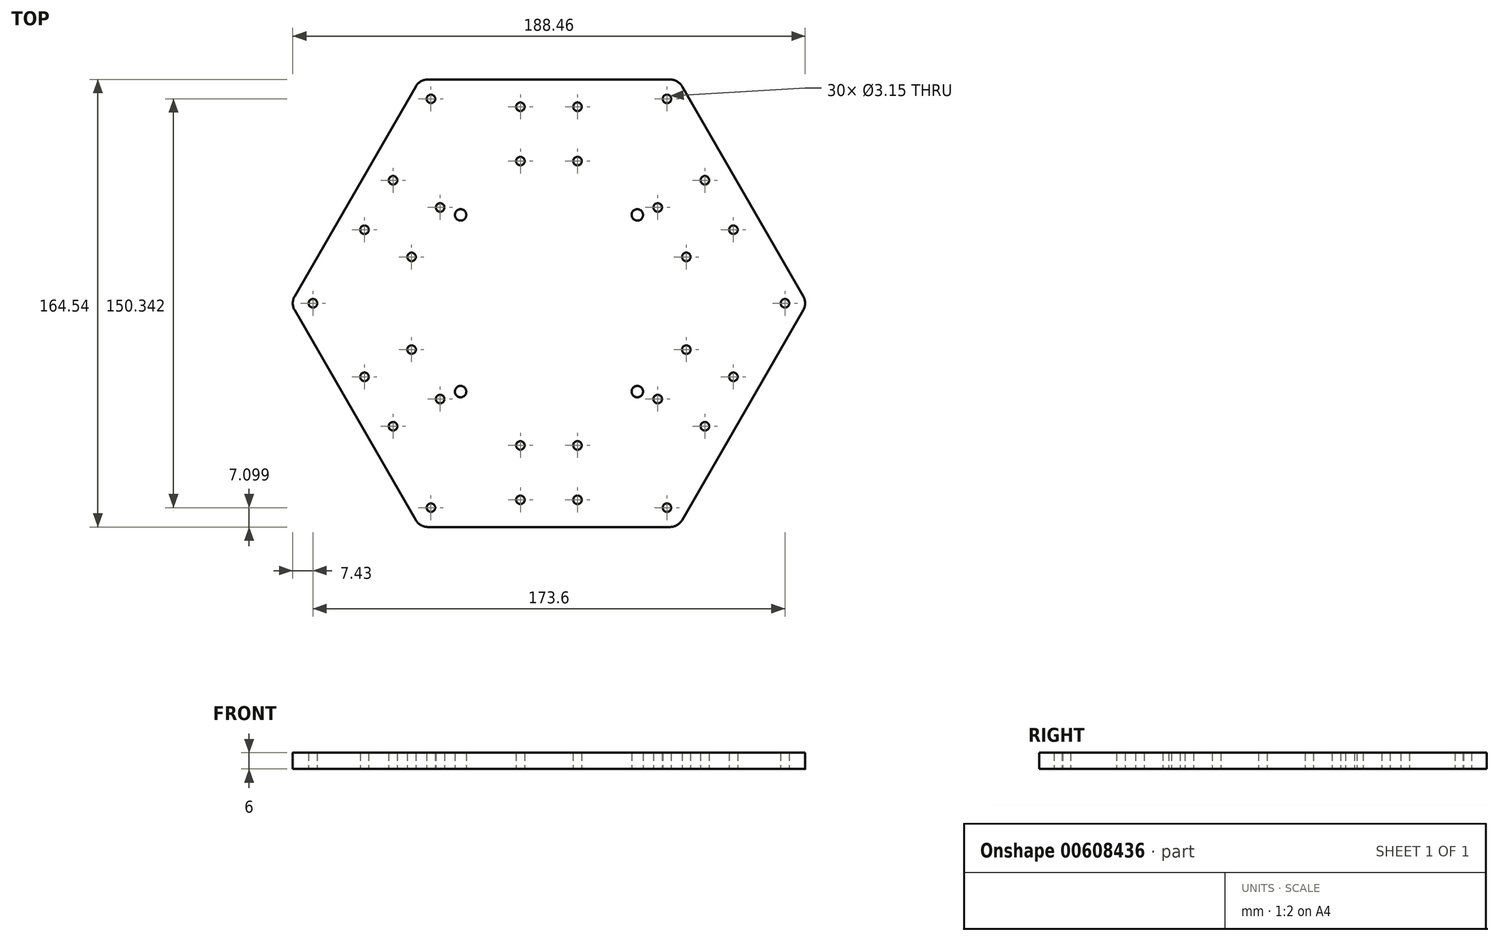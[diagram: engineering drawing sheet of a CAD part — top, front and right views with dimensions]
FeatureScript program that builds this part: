
annotation { "Feature Type Name" : "Feature", "Feature Type Description" : "" }
export const myFeature = defineFeature(function(context is Context, id is Id, definition is map)
    precondition{}
    {
        {
            var Q0;
            Q0=qCreatedBy(makeId("Top.planeOp"),FACE);
            var sketch = newSketch(context, id + "F0", { "sketchPlane" : qUnion([Q0])});
            skLineSegment(sketch, "E0.1", {"start": v(-48.94, -79.77) * mm, "end": v(-93.56, -2.5) * mm});
            skLineSegment(sketch, "E0.2", {"start": v(-93.56, 2.5) * mm, "end": v(-48.94, 79.77) * mm});
            skLineSegment(sketch, "E0.3", {"start": v(-44.61, 82.27) * mm, "end": v(44.61, 82.27) * mm});
            skLineSegment(sketch, "E0.4", {"start": v(48.94, 79.77) * mm, "end": v(93.56, 2.5) * mm});
            skLineSegment(sketch, "E0.5", {"start": v(93.56, -2.5) * mm, "end": v(48.94, -79.77) * mm});
            skPoint(sketch, "E0.cCircle.center.orphan", {"position": v(0, 0) * mm});
            skLineSegment(sketch, "E1", {"start": v(-44.61, -82.27) * mm, "end": v(44.61, -82.27) * mm});
            skPoint(sketch, "E2", {"position": v(-47.5, 82.27) * mm});
            skPoint(sketch, "E3", {"position": v(-43.4, 75.17) * mm});
            skCircle(sketch, "E4", {"center": v(-43.4, 75.17) * mm, "radius": 1.57 * mm});
            skCircle(sketch, "E5.1.0", {"center": v(-86.8, 0) * mm, "radius": 1.57 * mm});
            skCircle(sketch, "E5.2.0", {"center": v(-43.4, -75.17) * mm, "radius": 1.57 * mm});
            skCircle(sketch, "E5.3.0", {"center": v(43.4, -75.17) * mm, "radius": 1.57 * mm});
            skCircle(sketch, "E5.4.0", {"center": v(86.8, 0) * mm, "radius": 1.57 * mm});
            skCircle(sketch, "E5.5.0", {"center": v(43.4, 75.17) * mm, "radius": 1.57 * mm});
            skPoint(sketch, "E6", {"position": v(47.5, 82.27) * mm});
            skPoint(sketch, "E7", {"position": v(0, 82.27) * mm});
            skPoint(sketch, "E8", {"position": v(10.5, 82.27) * mm});
            skPoint(sketch, "E9", {"position": v(-10.5, 82.27) * mm});
            skPoint(sketch, "E10", {"position": v(-10.5, 72.27) * mm});
            skPoint(sketch, "E11", {"position": v(10.5, 72.27) * mm});
            skPoint(sketch, "E12", {"position": v(-10.5, 52.27) * mm});
            skPoint(sketch, "E13", {"position": v(10.5, 52.27) * mm});
            skCircle(sketch, "E14", {"center": v(-10.5, 72.27) * mm, "radius": 1.57 * mm});
            skCircle(sketch, "E15", {"center": v(10.5, 72.27) * mm, "radius": 1.57 * mm});
            skCircle(sketch, "E16", {"center": v(10.5, 52.27) * mm, "radius": 1.57 * mm});
            skCircle(sketch, "E17", {"center": v(-10.5, 52.27) * mm, "radius": 1.57 * mm});
            skPoint(sketch, "E18.1.0", {"position": v(-57.34, 45.23) * mm});
            skCircle(sketch, "E18.1.1", {"center": v(-57.34, 45.23) * mm, "radius": 1.57 * mm});
            skPoint(sketch, "E18.1.2", {"position": v(-67.84, 27.04) * mm});
            skCircle(sketch, "E18.1.3", {"center": v(-67.84, 27.04) * mm, "radius": 1.57 * mm});
            skPoint(sketch, "E18.1.4", {"position": v(-50.52, 17.04) * mm});
            skCircle(sketch, "E18.1.5", {"center": v(-50.52, 17.04) * mm, "radius": 1.57 * mm});
            skPoint(sketch, "E18.1.6", {"position": v(-40.02, 35.23) * mm});
            skCircle(sketch, "E18.1.7", {"center": v(-40.02, 35.23) * mm, "radius": 1.57 * mm});
            skPoint(sketch, "E18.2.0", {"position": v(-67.84, -27.04) * mm});
            skCircle(sketch, "E18.2.1", {"center": v(-67.84, -27.04) * mm, "radius": 1.57 * mm});
            skPoint(sketch, "E18.2.2", {"position": v(-57.34, -45.23) * mm});
            skCircle(sketch, "E18.2.3", {"center": v(-57.34, -45.23) * mm, "radius": 1.57 * mm});
            skPoint(sketch, "E18.2.4", {"position": v(-40.02, -35.23) * mm});
            skCircle(sketch, "E18.2.5", {"center": v(-40.02, -35.23) * mm, "radius": 1.57 * mm});
            skPoint(sketch, "E18.2.6", {"position": v(-50.52, -17.04) * mm});
            skCircle(sketch, "E18.2.7", {"center": v(-50.52, -17.04) * mm, "radius": 1.57 * mm});
            skPoint(sketch, "E18.3.0", {"position": v(-10.5, -72.27) * mm});
            skCircle(sketch, "E18.3.1", {"center": v(-10.5, -72.27) * mm, "radius": 1.57 * mm});
            skPoint(sketch, "E18.3.2", {"position": v(10.5, -72.27) * mm});
            skCircle(sketch, "E18.3.3", {"center": v(10.5, -72.27) * mm, "radius": 1.57 * mm});
            skPoint(sketch, "E18.3.4", {"position": v(10.5, -52.27) * mm});
            skCircle(sketch, "E18.3.5", {"center": v(10.5, -52.27) * mm, "radius": 1.57 * mm});
            skPoint(sketch, "E18.3.6", {"position": v(-10.5, -52.27) * mm});
            skCircle(sketch, "E18.3.7", {"center": v(-10.5, -52.27) * mm, "radius": 1.57 * mm});
            skPoint(sketch, "E18.4.0", {"position": v(57.34, -45.23) * mm});
            skCircle(sketch, "E18.4.1", {"center": v(57.34, -45.23) * mm, "radius": 1.57 * mm});
            skPoint(sketch, "E18.4.2", {"position": v(67.84, -27.04) * mm});
            skCircle(sketch, "E18.4.3", {"center": v(67.84, -27.04) * mm, "radius": 1.57 * mm});
            skPoint(sketch, "E18.4.4", {"position": v(50.52, -17.04) * mm});
            skCircle(sketch, "E18.4.5", {"center": v(50.52, -17.04) * mm, "radius": 1.57 * mm});
            skPoint(sketch, "E18.4.6", {"position": v(40.02, -35.23) * mm});
            skCircle(sketch, "E18.4.7", {"center": v(40.02, -35.23) * mm, "radius": 1.57 * mm});
            skPoint(sketch, "E18.5.0", {"position": v(67.84, 27.04) * mm});
            skCircle(sketch, "E18.5.1", {"center": v(67.84, 27.04) * mm, "radius": 1.57 * mm});
            skPoint(sketch, "E18.5.2", {"position": v(57.34, 45.23) * mm});
            skCircle(sketch, "E18.5.3", {"center": v(57.34, 45.23) * mm, "radius": 1.57 * mm});
            skPoint(sketch, "E18.5.4", {"position": v(40.02, 35.23) * mm});
            skCircle(sketch, "E18.5.5", {"center": v(40.02, 35.23) * mm, "radius": 1.57 * mm});
            skPoint(sketch, "E18.5.6", {"position": v(50.52, 17.04) * mm});
            skCircle(sketch, "E18.5.7", {"center": v(50.52, 17.04) * mm, "radius": 1.57 * mm});
            skPoint(sketch, "E19.left.end.orphan", {"position": v(32.5, 32.5) * mm});
            skPoint(sketch, "E19.bottom.start.orphan", {"position": v(32.5, -32.5) * mm});
            skPoint(sketch, "E19.right.end.orphan", {"position": v(-32.5, 32.5) * mm});
            skPoint(sketch, "E19.right.start.orphan", {"position": v(-32.5, -32.5) * mm});
            skCircle(sketch, "E20", {"center": v(-32.5, 32.5) * mm, "radius": 2.1 * mm});
            skCircle(sketch, "E21.1.1", {"center": v(-32.5, -32.5) * mm, "radius": 2.1 * mm});
            skCircle(sketch, "E21.2.1", {"center": v(32.5, -32.5) * mm, "radius": 2.1 * mm});
            skCircle(sketch, "E21.3.1", {"center": v(32.5, 32.5) * mm, "radius": 2.1 * mm});
            skPoint(sketch, "E22.visualSharp", {"position": v(47.5, -82.27) * mm});
            skArc(sketch, "E22.filletArc", {"start": v(44.61, -82.27) * mm, "mid": v(47.11, -81.6) * mm, "end": v(48.94, -79.77) * mm});
            skPoint(sketch, "E23.1.0", {"position": v(95, 0) * mm});
            skArc(sketch, "E23.1.1", {"start": v(93.56, -2.5) * mm, "mid": v(94.23, 0) * mm, "end": v(93.56, 2.5) * mm});
            skArc(sketch, "E23.2.1", {"start": v(48.94, 79.77) * mm, "mid": v(47.11, 81.6) * mm, "end": v(44.61, 82.27) * mm});
            skArc(sketch, "E23.3.1", {"start": v(-44.61, 82.27) * mm, "mid": v(-47.11, 81.6) * mm, "end": v(-48.94, 79.77) * mm});
            skPoint(sketch, "E23.4.0", {"position": v(-95, 0) * mm});
            skArc(sketch, "E23.4.1", {"start": v(-93.56, 2.5) * mm, "mid": v(-94.23, 0) * mm, "end": v(-93.56, -2.5) * mm});
            skPoint(sketch, "E23.5.0", {"position": v(-47.5, -82.27) * mm});
            skArc(sketch, "E23.5.1", {"start": v(-48.94, -79.77) * mm, "mid": v(-47.11, -81.6) * mm, "end": v(-44.61, -82.27) * mm});
            skSolve(sketch);
        }
        {
            var Q0;
            Q0=makeQuery(id+"F0.imprint","IMPRINT",FACE,{"disambiguationData":[TD([[makeQuery(id+"F0.imprint","IMPRINT",EDGE,{"derivedFrom":sQuery(id+"F0.wireOp",EDGE,"E0.1")}),-1.0]])]});
            extrude(context, id + "F1", {"entities" : qUnion([Q0]), "depth" : 6 * mm, "offsetDistance" : 25 * mm});
        }
    });
